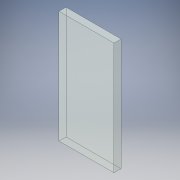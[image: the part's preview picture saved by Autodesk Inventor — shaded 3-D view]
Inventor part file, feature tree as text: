
AUTODESK INVENTOR PART (.ipt)
format: ipt  version: 2019 (Build 230136000, 136)  size: 105,984 bytes
history: native  units: in
note: dims shown in document units (in); Inventor stores cm internally (conversion verified against a paired STEP export)
features: extrude x1, sketch x1
ambient origin geometry x8: Origin, YZ Plane, XZ Plane, XY Plane, X Axis, Y Axis, Z Axis, Center Point
bodies: Solid1 (feature_tree)
feature tree (2):
  extrude  "Extrusion1"  Depth=0.05in TaperAngle=0.0deg
  sketch  "Sketch1"  dims[d0=0.391in d1=0.05in d2=0.0in]
